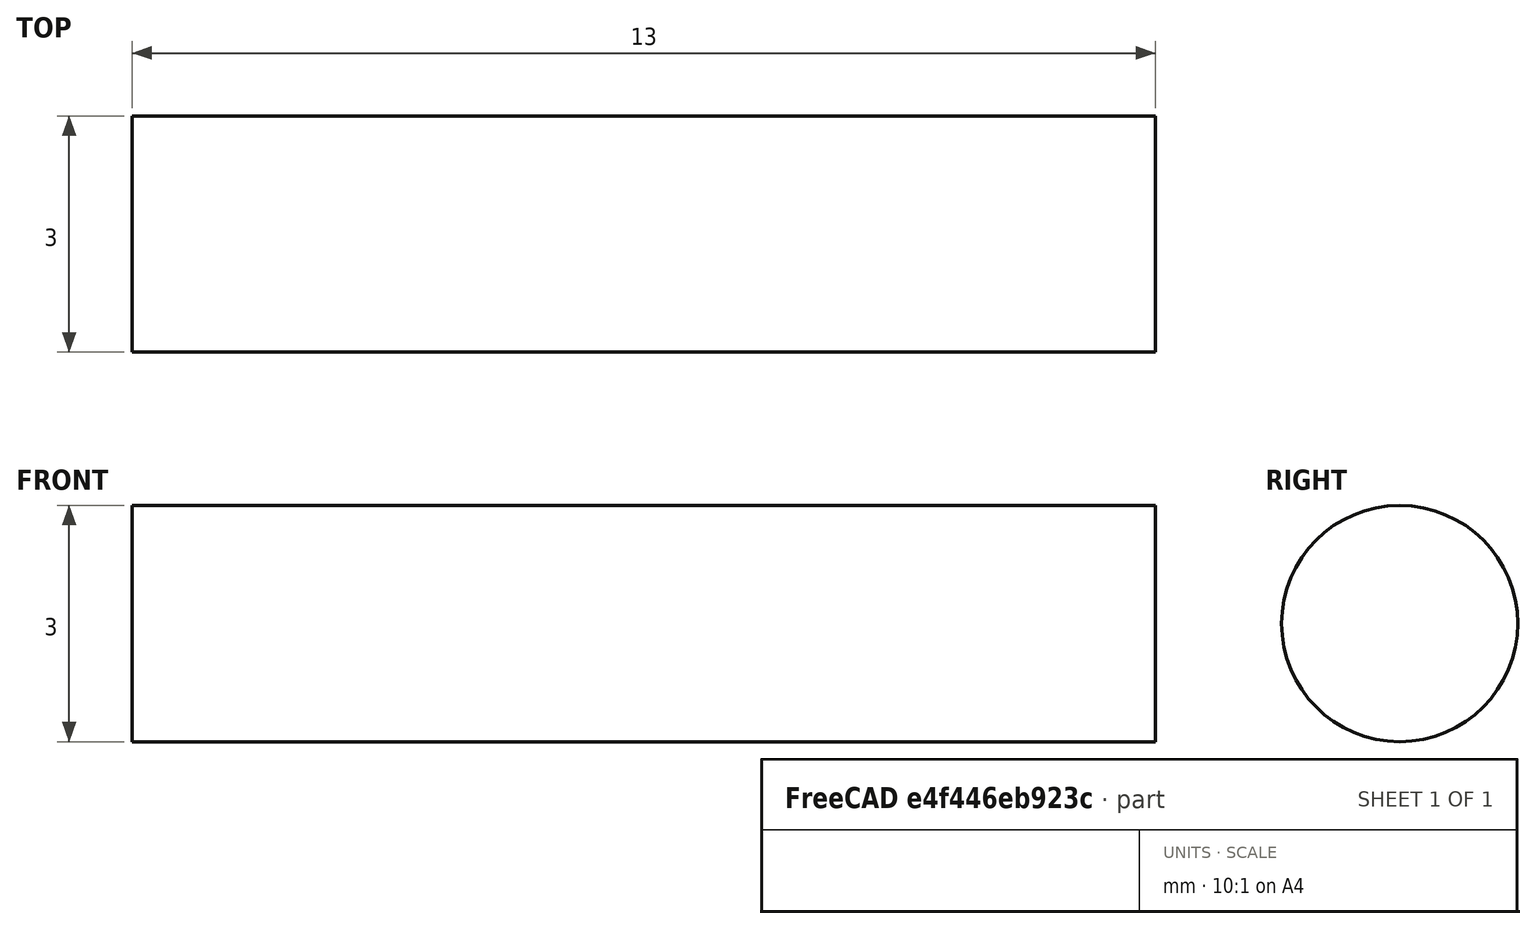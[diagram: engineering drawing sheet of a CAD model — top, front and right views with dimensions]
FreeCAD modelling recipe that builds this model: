
FCSTD DOCUMENT  (FreeCAD 0.21R33668 +26 (Git))
Label: shaft6_L13
License: All rights reserved
LicenseURL: https://en.wikipedia.org/wiki/All_rights_reserved
objects: Sketcher::SketchObject×1, PartDesign::Pad×1, PartDesign::Body×1
note: 4 computed .brp shape members not serialized (recipe doc carries the construction recipe); baked Part::Feature solids carry a one-line shape summary decoded from their .brp

FEATURE [Sketcher::SketchObject] Sketch
  FullyConstrained = true
  MapMode = 5
  Placement = pos=(0,0,0) rot=(0.57735,0.57735,0.57735;2.0944rad)
  Support = -> [YZ_Plane]
  sketch-geometry (1):
    g0: Circle CenterX=0 CenterY=0 CenterZ=0 NormalX=0 NormalY=0 NormalZ=1 AngleXU=0 Radius=1.5
  constraints (2):
    c: Coincident(g0,g-1)
    c: Diameter(g0) = 3
FEATURE [PartDesign::Pad] Pad
  Direction = (1,-2e-16,3e-16)
  Length = 13
  Length2 = 10
  Placement = pos=(0,0,0) rot=(1,1,1;2.0944rad)
  Profile = -> Sketch
  ReferenceAxis = -> Sketch [N_Axis]
  Type = 0
FEATURE [PartDesign::Body] Body
  Group = -> [Sketch,Pad]
  Origin = -> Origin
  Tip = -> Pad
